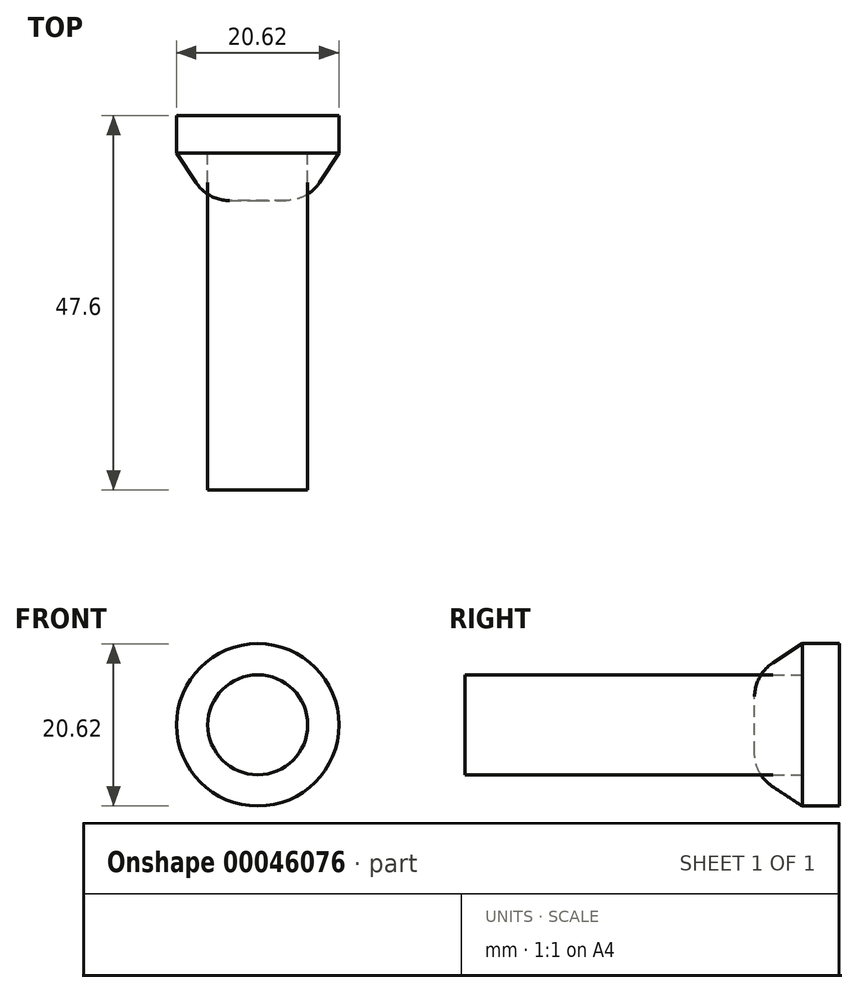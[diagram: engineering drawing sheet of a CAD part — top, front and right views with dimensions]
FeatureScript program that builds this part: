
annotation { "Feature Type Name" : "Feature", "Feature Type Description" : "" }
export const myFeature = defineFeature(function(context is Context, id is Id, definition is map)
    precondition{}
    {
        {
            var Q0;
            Q0=qCreatedBy(makeId("Front.planeOp"),FACE);
            var sketch = newSketch(context, id + "F0", { "sketchPlane" : qUnion([Q0])});
            skCircle(sketch, "E0", {"center": v(0, 0) * mm, "radius": 6.35 * mm});
            skCircle(sketch, "E1", {"center": v(0, 0) * mm, "radius": 10.31 * mm});
            skSolve(sketch);
        }
        {
            var Q0;
            Q0=makeQuery(id+"F0.imprint","IMPRINT",FACE,{"disambiguationData":[TD([[makeQuery(id+"F0.imprint","IMPRINT",EDGE,{"derivedFrom":sQuery(id+"F0.wireOp",EDGE,"E0")}),1.0]])]});
            extrude(context, id + "F1", {"entities" : qUnion([Q0]), "depth" : 42.85 * mm});
        }
        {
            var Q0;
            Q0=makeQuery(id+"F0.imprint","IMPRINT",FACE,{"disambiguationData":[TD([[makeQuery(id+"F0.imprint","IMPRINT",EDGE,{"derivedFrom":sQuery(id+"F0.wireOp",EDGE,"E0")}),1.0]])]});
            var Q1;
            Q1=makeQuery(id+"F0.imprint","IMPRINT",FACE,{"disambiguationData":[TD([[makeQuery(id+"F0.imprint","IMPRINT",EDGE,{"derivedFrom":sQuery(id+"F0.wireOp",EDGE,"E0")}),-1.0]])]});
            var Q2;
            Q2=sQuery(id+"F0.wireOp",EDGE,"E1");
            extrude(context, id + "F2", {"entities" : qUnion([Q0, Q1]), "surfaceEntities" : qUnion([Q2]), "oppositeDirection" : true, "depth" : 4.75 * mm});
        }
        {
            var Q0;
            Q0=qCreatedBy(makeId("Right.planeOp"),FACE);
            var sketch = newSketch(context, id + "F3", { "sketchPlane" : qUnion([Q0])});
            skLineSegment(sketch, "E2", {"start": v(0, 0) * mm, "end": v(-6.05, 0) * mm, "construction": true});
            skLineSegment(sketch, "E3", {"start": v(-6.05, 0) * mm, "end": v(0, 0) * mm, "construction": true});
            skSolve(sketch);
        }
        {
            var Q0;
            Q0=sQuery(id+"F3.wireOp",VERTEX,"E3.start");
            var Q1;
            Q1=qCreatedBy(makeId("Front.planeOp"),FACE);
            cPlane(context, id + "F4", {"entities" : qUnion([Q0, Q1]), "cplaneType" : CPlaneType.PLANE_POINT, "offset" : 152.4 * mm, "width" : 152.4 * mm, "height" : 152.4 * mm});
        }
        {
            var Q0;
            Q0=qCreatedBy(id+"F4.planeOp",FACE);
            var sketch = newSketch(context, id + "F5", { "sketchPlane" : qUnion([Q0])});
            skCircle(sketch, "E4", {"center": v(0, 0) * mm, "radius": 6.35 * mm});
            skSolve(sketch);
        }
        {
            var Q0;
            Q0=qCreatedBy(makeId("Front.planeOp"),FACE);
            var sketch = newSketch(context, id + "F6", { "sketchPlane" : qUnion([Q0])});
            skCircle(sketch, "E5", {"center": v(0, 0) * mm, "radius": 10.31 * mm});
            skSolve(sketch);
        }
        {
            var Q0;
            Q0 = qSketchRegion(id + "F5", true);
            var Q1;
            Q1 = qSketchRegion(id + "F6", true);
            loft(context, id + "F7", {"sheetProfilesArray" : [{ "sheetProfileEntities" : qUnion([Q0]) }, { "sheetProfileEntities" : qUnion([Q1]) }]});
        }
        {
            var Q0;
            Q0=makeQuery(id+"F7.opLoft","MID_CAP_EDGE",EDGE,{"disambiguationData":[OSD([sQuery(id+"F5.wireOp",EDGE,"E4")])],"capPos":0.0});
            fillet(context, id + "F8", {"entities" : qUnion([Q0]), "radius" : 5.08 * mm, "tangentPropagation" : true, "allowEdgeOverflow" : false});
        }
    });
